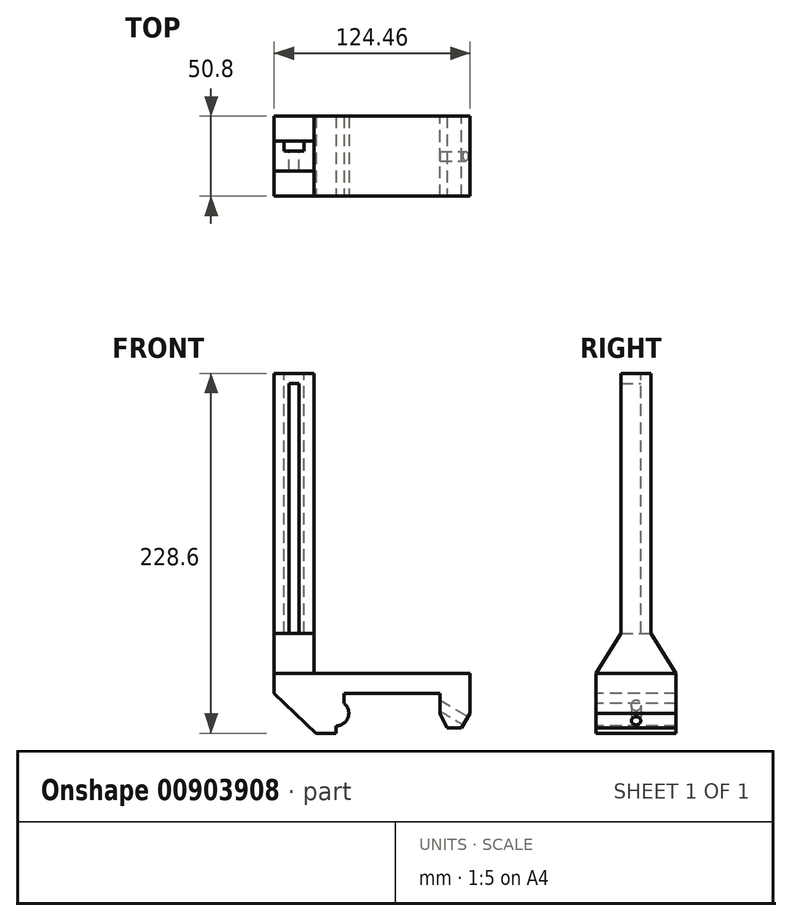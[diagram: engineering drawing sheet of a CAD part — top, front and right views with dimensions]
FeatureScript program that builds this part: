
annotation { "Feature Type Name" : "Feature", "Feature Type Description" : "" }
export const myFeature = defineFeature(function(context is Context, id is Id, definition is map)
    precondition{}
    {
        {
            var Q0;
            Q0=qCreatedBy(makeId("Front.planeOp"),FACE);
            var sketch = newSketch(context, id + "F0", { "sketchPlane" : qUnion([Q0])});
            skLineSegment(sketch, "E0.bottom", {"start": v(49.53, -19.05) * mm, "end": v(-49.53, -19.05) * mm});
            skLineSegment(sketch, "E0.top", {"start": v(49.53, 19.05) * mm, "end": v(-49.53, 19.05) * mm});
            skLineSegment(sketch, "E0.left", {"start": v(49.53, -19.05) * mm, "end": v(49.53, 19.05) * mm});
            skLineSegment(sketch, "E0.right", {"start": v(-49.53, -19.05) * mm, "end": v(-49.53, 19.05) * mm});
            skPoint(sketch, "E0.middle", {"position": v(0, 0) * mm});
            skLineSegment(sketch, "E1.bottom", {"start": v(30.48, -44.45) * mm, "end": v(-30.48, -44.45) * mm});
            skLineSegment(sketch, "E1.top", {"start": v(30.48, 6.35) * mm, "end": v(-30.48, 6.35) * mm});
            skLineSegment(sketch, "E1.left", {"start": v(30.48, -44.45) * mm, "end": v(30.48, 6.35) * mm});
            skLineSegment(sketch, "E1.right", {"start": v(-30.48, -44.45) * mm, "end": v(-30.48, 6.35) * mm});
            skPoint(sketch, "E1.middle", {"position": v(0, -19.05) * mm});
            skSolve(sketch);
        }
        {
            var Q0;
            Q0=makeQuery(id+"F0.imprint","IMPRINT",FACE,{"disambiguationData":[TD([[makeQuery(id+"F0.imprint","IMPRINT",EDGE,{"derivedFrom":sQuery(id+"F0.wireOp",EDGE,"E0.top")}),1.0]])]});
            extrude(context, id + "F1", {"entities" : qUnion([Q0]), "endBound" : BoundingType.SYMMETRIC, "depth" : 50.8 * mm, "offsetDistance" : 25.4 * mm});
        }
        {
            var Q0;
            Q0=qCreatedBy(makeId("Front.planeOp"),FACE);
            var sketch = newSketch(context, id + "F2", { "sketchPlane" : qUnion([Q0])});
            skLineSegment(sketch, "E2.bottom", {"start": v(35.56, -33.74) * mm, "end": v(-35.56, -33.74) * mm});
            skLineSegment(sketch, "E2.top", {"start": v(35.56, -6.35) * mm, "end": v(-35.56, -6.35) * mm});
            skLineSegment(sketch, "E2.left", {"start": v(35.56, -33.74) * mm, "end": v(35.56, -6.35) * mm});
            skLineSegment(sketch, "E2.right", {"start": v(-35.56, -33.74) * mm, "end": v(-35.56, -6.35) * mm});
            skPoint(sketch, "E2.middle", {"position": v(0, -20.05) * mm});
            skSolve(sketch);
        }
        {
            var Q0;
            Q0=makeQuery(id+"F2.imprint","IMPRINT",FACE,{"disambiguationData":[TD([[makeQuery(id+"F2.imprint","IMPRINT",EDGE,{"derivedFrom":sQuery(id+"F2.wireOp",EDGE,"E2.bottom")}),-1.0]])]});
            extrude(context, id + "F3", {"entities" : qUnion([Q0]), "operationType" : NewBodyOperationType.REMOVE, "endBound" : BoundingType.SYMMETRIC, "oppositeDirection" : true, "depth" : 101.6 * mm, "offsetDistance" : 25.4 * mm});
        }
        {
            var Q0;
            Q0=makeQuery(id+"FqtUo2dF14dtISF_1.boolean.opBoolean","MERGE",FACE,{"derivedFrom":[makeQuery(id+"F1.opExtrude","CAP_FACE",FACE,{"disambiguationData":[OSD([sQuery(id+"F0.wireOp",EDGE,"E0.bottom"),sQuery(id+"F0.wireOp",EDGE,"E0.top"),sQuery(id+"F0.wireOp",EDGE,"E0.left"),sQuery(id+"F0.wireOp",EDGE,"E0.right"),sQuery(id+"F0.wireOp",EDGE,"E1.top"),sQuery(id+"F0.wireOp",EDGE,"E1.left"),sQuery(id+"F0.wireOp",EDGE,"E1.right")])],"isStart":false}),makeQuery(id+"FqtUo2dF14dtISF_1.opExtrude","CAP_FACE",FACE,{"disambiguationData":[OSD([sQuery(id+"Fa6pJ2o9r3T1tcu_1.wireOp",EDGE,"9ab49e5e-e781-4880-a481-f387394318e1.bottom"),sQuery(id+"Fa6pJ2o9r3T1tcu_1.wireOp",EDGE,"9ab49e5e-e781-4880-a481-f387394318e1.top"),sQuery(id+"Fa6pJ2o9r3T1tcu_1.wireOp",EDGE,"9ab49e5e-e781-4880-a481-f387394318e1.left"),sQuery(id+"Fa6pJ2o9r3T1tcu_1.wireOp",EDGE,"HMghRU8G-1H3M-OJ5W-wMgI-K1z1DDckNYTP"),sQuery(id+"Fa6pJ2o9r3T1tcu_1.wireOp",EDGE,"0KJWoq3j-ts2y-bZzM-44IR-2JegtjsgD1qJ")])],"isStart":true})]});
            var sketch = newSketch(context, id + "F4", { "sketchPlane" : qUnion([Q0])});
            skCircle(sketch, "E3", {"center": v(-35.56, -6.35) * mm, "radius": 8.06 * mm});
            skSolve(sketch);
        }
        {
            var Q0;
            Q0=qSketchRegion(id+"F4",true);
            extrude(context, id + "F5", {"entities" : qUnion([Q0]), "operationType" : NewBodyOperationType.ADD, "oppositeDirection" : true, "depth" : 50.8 * mm, "offsetDistance" : 25.4 * mm});
        }
        {
            var Q0;
            Q0=makeQuery(id+"F5.boolean.opBoolean","MERGE",FACE,{"derivedFrom":[makeQuery(id+"FqtUo2dF14dtISF_1.boolean.opBoolean","MERGE",FACE,{"derivedFrom":[makeQuery(id+"F1.opExtrude","CAP_FACE",FACE,{"disambiguationData":[OSD([sQuery(id+"F0.wireOp",EDGE,"E0.bottom"),sQuery(id+"F0.wireOp",EDGE,"E0.top"),sQuery(id+"F0.wireOp",EDGE,"E0.left"),sQuery(id+"F0.wireOp",EDGE,"E0.right"),sQuery(id+"F0.wireOp",EDGE,"E1.top"),sQuery(id+"F0.wireOp",EDGE,"E1.left"),sQuery(id+"F0.wireOp",EDGE,"E1.right")])],"isStart":false}),makeQuery(id+"FqtUo2dF14dtISF_1.opExtrude","CAP_FACE",FACE,{"disambiguationData":[OSD([sQuery(id+"Fa6pJ2o9r3T1tcu_1.wireOp",EDGE,"9ab49e5e-e781-4880-a481-f387394318e1.bottom"),sQuery(id+"Fa6pJ2o9r3T1tcu_1.wireOp",EDGE,"9ab49e5e-e781-4880-a481-f387394318e1.top"),sQuery(id+"Fa6pJ2o9r3T1tcu_1.wireOp",EDGE,"9ab49e5e-e781-4880-a481-f387394318e1.left"),sQuery(id+"Fa6pJ2o9r3T1tcu_1.wireOp",EDGE,"HMghRU8G-1H3M-OJ5W-wMgI-K1z1DDckNYTP"),sQuery(id+"Fa6pJ2o9r3T1tcu_1.wireOp",EDGE,"0KJWoq3j-ts2y-bZzM-44IR-2JegtjsgD1qJ")])],"isStart":true})]}),makeQuery(id+"F5.opExtrude","CAP_FACE",FACE,{"disambiguationData":[OSD([sQuery(id+"F4.wireOp",EDGE,"E3")])],"isStart":true})]});
            var sketch = newSketch(context, id + "F6", { "sketchPlane" : qUnion([Q0])});
            skLineSegment(sketch, "E4", {"start": v(35.56, -6.35) * mm, "end": v(35.56, -17.47) * mm});
            skLineSegment(sketch, "E5", {"start": v(35.56, -17.47) * mm, "end": v(30.48, -6.35) * mm});
            skLineSegment(sketch, "E6", {"start": v(30.48, -6.35) * mm, "end": v(35.56, -6.35) * mm});
            skSolve(sketch);
        }
        {
            var Q0;
            Q0=qSketchRegion(id+"F6",true);
            extrude(context, id + "F7", {"entities" : qUnion([Q0]), "operationType" : NewBodyOperationType.ADD, "oppositeDirection" : true, "depth" : 50.8 * mm, "offsetDistance" : 25.4 * mm});
        }
        {
            var Q0;
            Q0=makeQuery(id+"F1.opExtrude","SWEPT_FACE",FACE,{"disambiguationData":[OSD([sQuery(id+"F0.wireOp",EDGE,"E0.top")])]});
            var sketch = newSketch(context, id + "F8", { "sketchPlane" : qUnion([Q0])});
            skLineSegment(sketch, "E7.bottom", {"start": v(-49.53, 25.4) * mm, "end": v(-74.93, 25.4) * mm});
            skLineSegment(sketch, "E7.top", {"start": v(-49.53, -25.4) * mm, "end": v(-74.93, -25.4) * mm});
            skLineSegment(sketch, "E7.left", {"start": v(-49.53, 25.4) * mm, "end": v(-49.53, -25.4) * mm});
            skLineSegment(sketch, "E7.right", {"start": v(-74.93, 25.4) * mm, "end": v(-74.93, -25.4) * mm});
            skSolve(sketch);
        }
        {
            var Q0;
            Q0=makeQuery(id+"F8.imprint","IMPRINT",FACE,{"disambiguationData":[TD([[makeQuery(id+"F8.imprint","IMPRINT",EDGE,{"derivedFrom":sQuery(id+"F8.wireOp",EDGE,"E7.bottom")}),1.0]])]});
            extrude(context, id + "F9", {"entities" : qUnion([Q0]), "operationType" : NewBodyOperationType.ADD, "oppositeDirection" : true, "depth" : 38.1 * mm, "offsetDistance" : 25.4 * mm});
        }
        {
            var Q0;
            Q0=makeQuery(id+"F9.boolean.opBoolean","MERGE",FACE,{"derivedFrom":[makeQuery(id+"F1.opExtrude","SWEPT_FACE",FACE,{"disambiguationData":[OSD([sQuery(id+"F0.wireOp",EDGE,"E0.top")])]}),makeQuery(id+"F9.opExtrude","CAP_FACE",FACE,{"disambiguationData":[OSD([sQuery(id+"F8.wireOp",EDGE,"E7.bottom"),sQuery(id+"F8.wireOp",EDGE,"E7.top"),sQuery(id+"F8.wireOp",EDGE,"E7.left"),sQuery(id+"F8.wireOp",EDGE,"E7.right")])],"isStart":true})]});
            var sketch = newSketch(context, id + "F10", { "sketchPlane" : qUnion([Q0])});
            skLineSegment(sketch, "E8.bottom", {"start": v(-49.53, -9.53) * mm, "end": v(-74.93, -9.53) * mm});
            skLineSegment(sketch, "E8.top", {"start": v(-49.53, 9.52) * mm, "end": v(-74.93, 9.52) * mm});
            skLineSegment(sketch, "E8.left", {"start": v(-49.53, -9.53) * mm, "end": v(-49.53, 9.52) * mm});
            skLineSegment(sketch, "E8.right", {"start": v(-74.93, -9.53) * mm, "end": v(-74.93, 9.52) * mm});
            skPoint(sketch, "E8.middle", {"position": v(-62.23, 0) * mm});
            skSolve(sketch);
        }
        {
            var Q0;
            Q0 = qSketchRegion(id + "F10", true);
            extrude(context, id + "F11", {"entities" : qUnion([Q0]), "operationType" : NewBodyOperationType.ADD, "depth" : 190.5 * mm, "offsetDistance" : 25.4 * mm});
        }
        {
            var Q0;
            Q0=makeQuery(id+"F11.opExtrude","SWEPT_FACE",FACE,{"disambiguationData":[OSD([sQuery(id+"F10.wireOp",EDGE,"E8.top")])]});
            var sketch = newSketch(context, id + "F12", { "sketchPlane" : qUnion([Q0])});
            skLineSegment(sketch, "E9.bottom", {"start": v(68.58, 44.45) * mm, "end": v(55.88, 44.45) * mm});
            skLineSegment(sketch, "E9.top", {"start": v(68.58, 209.55) * mm, "end": v(55.88, 209.55) * mm});
            skLineSegment(sketch, "E9.left", {"start": v(68.58, 44.45) * mm, "end": v(68.58, 209.55) * mm});
            skLineSegment(sketch, "E9.right", {"start": v(55.88, 44.45) * mm, "end": v(55.88, 209.55) * mm});
            skPoint(sketch, "E9.middle", {"position": v(62.23, 127) * mm});
            skSolve(sketch);
        }
        {
            var Q0;
            Q0 = qSketchRegion(id + "F12", true);
            extrude(context, id + "F13", {"entities" : qUnion([Q0]), "operationType" : NewBodyOperationType.REMOVE, "oppositeDirection" : true, "depth" : 6.35 * mm, "offsetDistance" : 25.4 * mm});
        }
        {
            var Q0;
            Q0=makeQuery(id+"F13.boolean.opBoolean","COPY",FACE,{"derivedFrom":makeQuery(id+"F13.opExtrude","CAP_FACE",FACE,{"disambiguationData":[OSD([sQuery(id+"F12.wireOp",EDGE,"E9.bottom"),sQuery(id+"F12.wireOp",EDGE,"E9.top"),sQuery(id+"F12.wireOp",EDGE,"E9.left"),sQuery(id+"F12.wireOp",EDGE,"E9.right")])],"isStart":false})});
            var sketch = newSketch(context, id + "F14", { "sketchPlane" : qUnion([Q0])});
            skLineSegment(sketch, "E10.bottom", {"start": v(65.4, 44.45) * mm, "end": v(59.06, 44.45) * mm});
            skLineSegment(sketch, "E10.top", {"start": v(65.4, 203.2) * mm, "end": v(59.05, 203.2) * mm});
            skLineSegment(sketch, "E10.left", {"start": v(65.4, 44.45) * mm, "end": v(65.4, 203.2) * mm});
            skLineSegment(sketch, "E10.right", {"start": v(59.06, 44.45) * mm, "end": v(59.05, 203.2) * mm});
            skPoint(sketch, "E10.middle", {"position": v(62.23, 123.83) * mm});
            skSolve(sketch);
        }
        {
            var Q0;
            Q0 = qSketchRegion(id + "F14", true);
            extrude(context, id + "F15", {"entities" : qUnion([Q0]), "operationType" : NewBodyOperationType.REMOVE, "endBound" : BoundingType.THROUGH_ALL, "oppositeDirection" : true, "depth" : 25.4 * mm, "offsetDistance" : 25.4 * mm});
        }
        {
            var Q0;
            Q0=makeQuery(id+"F11.boolean.opBoolean","MERGE",FACE,{"derivedFrom":[makeQuery(id+"F9.opExtrude","SWEPT_FACE",FACE,{"disambiguationData":[OSD([sQuery(id+"F8.wireOp",EDGE,"E7.right")])]}),makeQuery(id+"F11.opExtrude","SWEPT_FACE",FACE,{"disambiguationData":[OSD([sQuery(id+"F10.wireOp",EDGE,"E8.right")])]})]});
            var sketch = newSketch(context, id + "F16", { "sketchPlane" : qUnion([Q0])});
            skLineSegment(sketch, "E11", {"start": v(-9.52, 19.05) * mm, "end": v(-9.52, 44.45) * mm});
            skLineSegment(sketch, "E12", {"start": v(-9.52, 19.05) * mm, "end": v(-25.4, 19.05) * mm});
            skLineSegment(sketch, "E13", {"start": v(-25.4, 19.05) * mm, "end": v(-9.52, 44.45) * mm});
            skLineSegment(sketch, "E14", {"start": v(9.53, 19.05) * mm, "end": v(9.53, 44.45) * mm});
            skLineSegment(sketch, "E15", {"start": v(9.53, 19.05) * mm, "end": v(25.4, 19.05) * mm});
            skLineSegment(sketch, "E16", {"start": v(25.4, 19.05) * mm, "end": v(9.53, 44.45) * mm});
            skSolve(sketch);
        }
        {
            var Q0;
            Q0 = qSketchRegion(id + "F16", true);
            extrude(context, id + "F17", {"entities" : qUnion([Q0]), "operationType" : NewBodyOperationType.ADD, "oppositeDirection" : true, "depth" : 25.4 * mm, "offsetDistance" : 25.4 * mm});
        }
        {
            var Q0;
            Q0=makeQuery(id+"F9.boolean.opBoolean","MERGE",FACE,{"derivedFrom":[makeQuery(id+"F7.boolean.opBoolean","MERGE",FACE,{"derivedFrom":[makeQuery(id+"F5.boolean.opBoolean","MERGE",FACE,{"derivedFrom":[makeQuery(id+"F1.opExtrude","CAP_FACE",FACE,{"disambiguationData":[OSD([sQuery(id+"F0.wireOp",EDGE,"E0.bottom"),sQuery(id+"F0.wireOp",EDGE,"E0.top"),sQuery(id+"F0.wireOp",EDGE,"E0.left"),sQuery(id+"F0.wireOp",EDGE,"E0.right"),sQuery(id+"F0.wireOp",EDGE,"E1.top"),sQuery(id+"F0.wireOp",EDGE,"E1.left"),sQuery(id+"F0.wireOp",EDGE,"E1.right")])],"isStart":false}),makeQuery(id+"F5.opExtrude","CAP_FACE",FACE,{"disambiguationData":[OSD([sQuery(id+"F4.wireOp",EDGE,"E3")])],"isStart":true})]}),makeQuery(id+"F7.opExtrude","CAP_FACE",FACE,{"disambiguationData":[OSD([sQuery(id+"F6.wireOp",EDGE,"E4"),sQuery(id+"F6.wireOp",EDGE,"E5"),sQuery(id+"F6.wireOp",EDGE,"E6")])],"isStart":true})]}),makeQuery(id+"F9.opExtrude","SWEPT_FACE",FACE,{"disambiguationData":[OSD([sQuery(id+"F8.wireOp",EDGE,"E7.top")])]})]});
            var sketch = newSketch(context, id + "F18", { "sketchPlane" : qUnion([Q0])});
            skLineSegment(sketch, "E17", {"start": v(-74.93, 6.35) * mm, "end": v(-48.26, -19.05) * mm});
            skLineSegment(sketch, "E18", {"start": v(-48.26, -19.05) * mm, "end": v(-74.93, -19.05) * mm});
            skLineSegment(sketch, "E19", {"start": v(-74.93, -19.05) * mm, "end": v(-74.93, 6.35) * mm});
            skSolve(sketch);
        }
        {
            var Q0;
            Q0=makeQuery(id+"F18.imprint","IMPRINT",FACE,{"disambiguationData":[TD([[makeQuery(id+"F18.imprint","IMPRINT",EDGE,{"derivedFrom":sQuery(id+"F18.wireOp",EDGE,"E17")}),-1.0]])]});
            extrude(context, id + "F19", {"entities" : qUnion([Q0]), "operationType" : NewBodyOperationType.REMOVE, "endBound" : BoundingType.THROUGH_ALL, "oppositeDirection" : true, "depth" : 25.4 * mm, "offsetDistance" : 25.4 * mm});
        }
        {
            var Q0;
            {var subQ5=sQuery(id+"F0.wireOp",EDGE,"E0.top");Q0=makeQuery(id+"F4.imprint","IMPRINT",FACE,{"disambiguationData":[TD([[makeQuery(id+"F4.imprint","IMPRINT",EDGE,{"derivedFrom":makeQuery(id+"F1.opExtrude","CAP_EDGE",EDGE,{"disambiguationData":[OSD([subQ5])],"isStart":false})}),1.0]])]});}
            var sketch = newSketch(context, id + "F20", { "sketchPlane" : qUnion([Q0])});
            skLineSegment(sketch, "E20", {"start": v(49.53, -6.35) * mm, "end": v(49.53, -19.05) * mm});
            skLineSegment(sketch, "E21", {"start": v(49.53, -19.05) * mm, "end": v(41.9, -19.05) * mm});
            skLineSegment(sketch, "E22", {"start": v(49.53, -6.35) * mm, "end": v(41.9, -19.05) * mm});
            skSolve(sketch);
        }
        {
            var Q0;
            Q0 = qSketchRegion(id + "F20", true);
            extrude(context, id + "F21", {"entities" : qUnion([Q0]), "operationType" : NewBodyOperationType.REMOVE, "endBound" : BoundingType.THROUGH_ALL, "oppositeDirection" : true, "depth" : 25.4 * mm, "offsetDistance" : 25.4 * mm});
        }
        {
            var Q0;
            {var subQ5=sQuery(id+"F0.wireOp",EDGE,"E0.top");Q0=makeQuery(id+"F4.imprint","IMPRINT",FACE,{"disambiguationData":[TD([[makeQuery(id+"F4.imprint","IMPRINT",EDGE,{"derivedFrom":makeQuery(id+"F1.opExtrude","CAP_EDGE",EDGE,{"disambiguationData":[OSD([subQ5])],"isStart":false})}),1.0]])]});}
            var sketch = newSketch(context, id + "F22", { "sketchPlane" : qUnion([Q0])});
            skLineSegment(sketch, "E23.bottom", {"start": v(46.12, -15.56) * mm, "end": v(32.46, -15.56) * mm});
            skLineSegment(sketch, "E23.top", {"start": v(46.12, -23.73) * mm, "end": v(32.46, -23.73) * mm});
            skLineSegment(sketch, "E23.left", {"start": v(46.12, -15.56) * mm, "end": v(46.12, -23.73) * mm});
            skLineSegment(sketch, "E23.right", {"start": v(32.46, -15.56) * mm, "end": v(32.46, -23.73) * mm});
            skPoint(sketch, "E23.middle", {"position": v(39.29, -19.64) * mm});
            skSolve(sketch);
        }
        {
            var Q0;
            Q0 = qSketchRegion(id + "F22", true);
            extrude(context, id + "F23", {"entities" : qUnion([Q0]), "operationType" : NewBodyOperationType.REMOVE, "endBound" : BoundingType.THROUGH_ALL, "oppositeDirection" : true, "depth" : 25.4 * mm, "offsetDistance" : 25.4 * mm});
        }
        {
            var Q0;
            Q0=makeQuery(id+"F21.boolean.opBoolean","COPY",FACE,{"derivedFrom":makeQuery(id+"F21.opExtrude","SWEPT_FACE",FACE,{"disambiguationData":[OSD([sQuery(id+"F20.wireOp",EDGE,"E22")])]})});
            var sketch = newSketch(context, id + "F24", { "sketchPlane" : qUnion([Q0])});
            skCircle(sketch, "E24", {"center": v(0, 14.48) * mm, "radius": 3 * mm});
            skSolve(sketch);
        }
        {
            var Q0;
            Q0 = qSketchRegion(id + "F24", true);
            extrude(context, id + "F25", {"entities" : qUnion([Q0]), "operationType" : NewBodyOperationType.REMOVE, "endBound" : BoundingType.UP_TO_NEXT, "oppositeDirection" : true, "depth" : 25.4 * mm, "offsetDistance" : 25.4 * mm});
        }
    });
